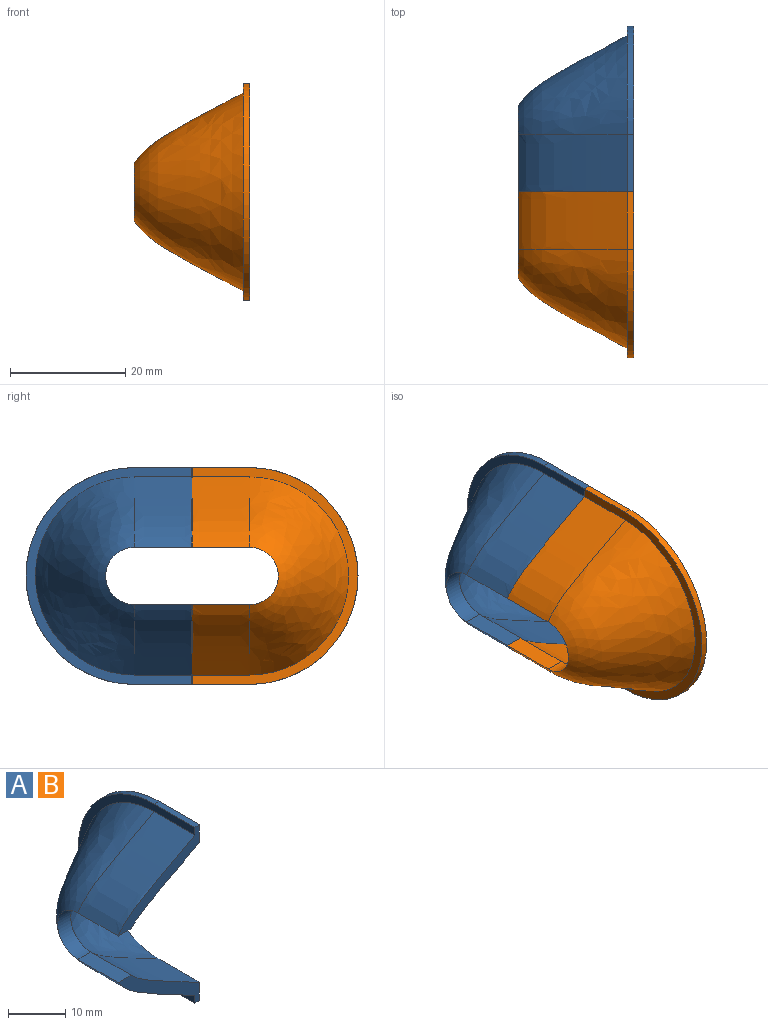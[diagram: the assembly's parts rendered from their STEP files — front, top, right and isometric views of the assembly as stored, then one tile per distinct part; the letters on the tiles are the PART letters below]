
ASSEMBLY  parts=2 mates=1
PART A: 16 faces, bbox 20.1x28.9x37.7 mm
  f0: cylinder r=5mm len=10mm, axis (1,0,0), area 50.5mm2, adj f1,f5,f6,f11
  f1: revolved ~30x16.92mm, area 637.4mm2, adj f0,f2,f7,f14
  f2: plane 37.72x28.86mm, normal (1,0,0), area 282.4mm2, adj f1,f3,f7,f8,f10,f13,f14,f15
  f3: cone r=18.86mm half-angle=0.6deg, axis (1,0,0), area 68.8mm2, adj f2,f4,f8,f13
  f4: plane 37.69x28.85mm, normal (-1,0,0), area 125.1mm2, adj f3,f5,f8,f9,f10,f12,f13,f15
  f5: revolved ~34.43x18.97mm, area 834mm2, adj f0,f4,f9,f12
  f6: plane 10x3.21mm, normal (0,0,-1), area 32.1mm2, adj f0,f7,f9,f10
  f7: extruded ~16.92x10mm, area 197.1mm2, adj f1,f2,f6,f10
  f8: plane 10x1.16mm, normal (-0.01,0,1), area 11.6mm2, adj f2,f3,f4,f10
  f9: extruded ~18.97x12.21mm, area 227.6mm2, adj f4,f5,f6,f10
  f10: plane 20.13x13.86mm, normal (0,-1,0), area 56.3mm2, adj f2,f4,f6,f7,f8,f9
  f11: plane 10x3.21mm, normal (0,0,1), area 32.1mm2, adj f0,f12,f14,f15
  f12: extruded ~18.97x12.21mm, area 227.6mm2, adj f4,f5,f11,f15
  f13: plane 10x1.16mm, normal (-0.01,0,-1), area 11.6mm2, adj f2,f3,f4,f15
  f14: extruded ~16.92x10mm, area 197.1mm2, adj f1,f2,f11,f15
  f15: plane 20.13x13.86mm, normal (0,-1,0), area 56.3mm2, adj f2,f4,f11,f12,f13,f14
PART B: same geometry as A
PLACE A t=(-5.81,-8.37,13.61)mm
PLACE B rot(axis=(-1,0,0),180deg) t=(-5.81,-28.37,17.95)mm
MATE fastened B.f10 <-> A.f15  axis (0,1,0) through (-24.35,-18.37,4.42)mm
